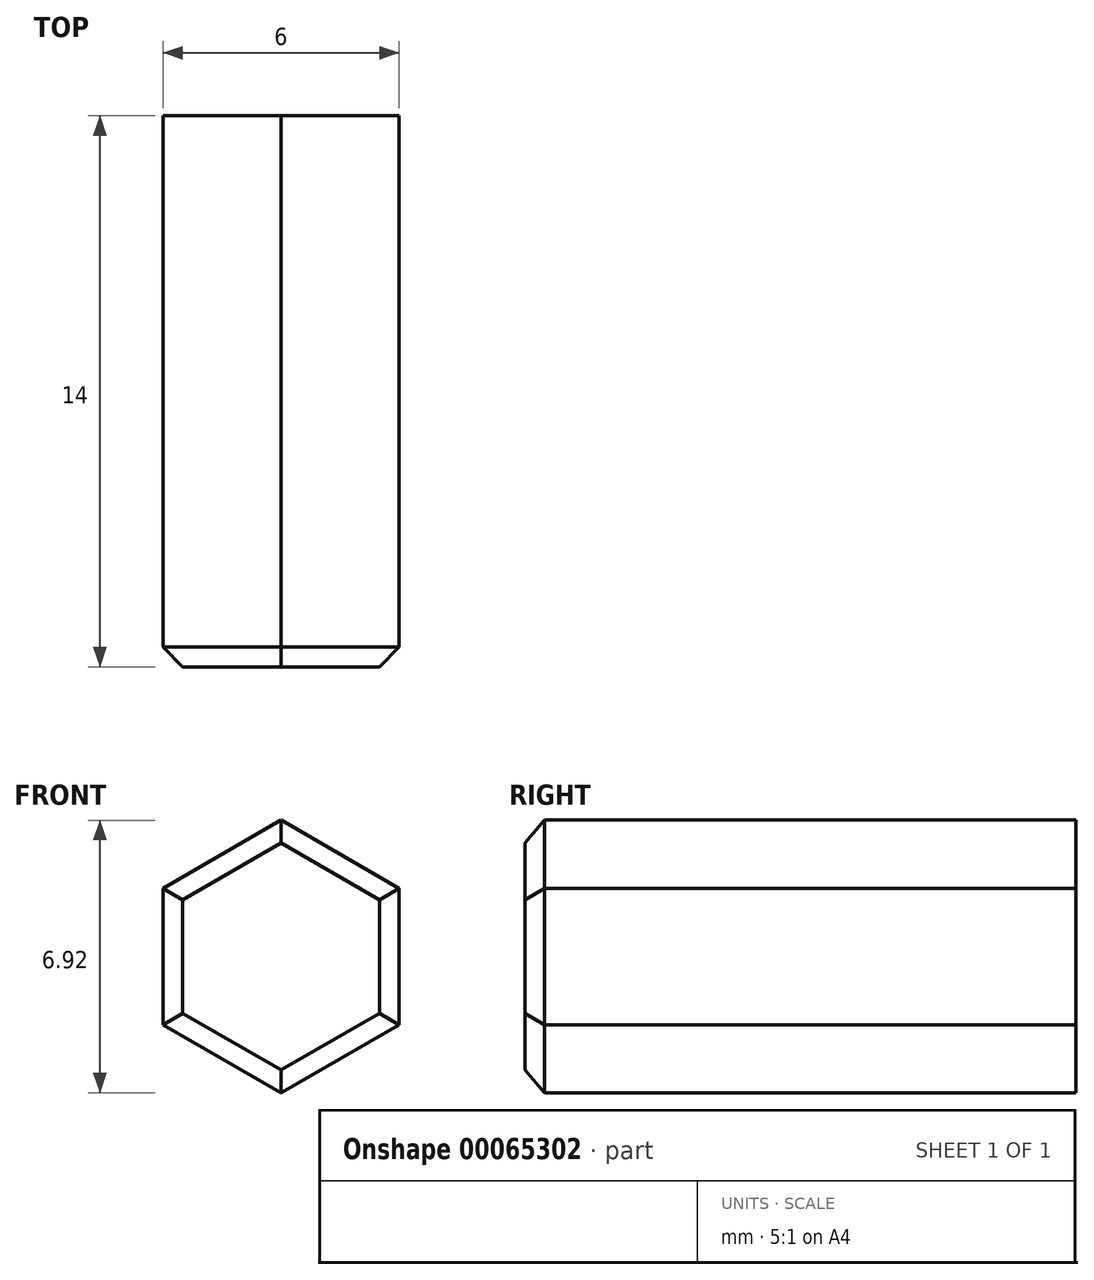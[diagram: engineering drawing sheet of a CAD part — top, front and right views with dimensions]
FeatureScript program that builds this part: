
annotation { "Feature Type Name" : "Feature", "Feature Type Description" : "" }
export const myFeature = defineFeature(function(context is Context, id is Id, definition is map)
    precondition{}
    {
        {
            var Q0;
            Q0=qCreatedBy(makeId("Front.planeOp"),FACE);
            var sketch = newSketch(context, id + "F0", { "sketchPlane" : qUnion([Q0])});
            skCircle(sketch, "E0.cCircle", {"center": v(0, 0) * mm, "radius": 3 * mm, "construction": true});
            skLineSegment(sketch, "E0.0", {"start": v(3, 1.73) * mm, "end": v(3, -1.73) * mm});
            skLineSegment(sketch, "E0.1", {"start": v(3, -1.73) * mm, "end": v(0, -3.46) * mm});
            skLineSegment(sketch, "E0.2", {"start": v(0, -3.46) * mm, "end": v(-3, -1.73) * mm});
            skLineSegment(sketch, "E0.3", {"start": v(-3, -1.73) * mm, "end": v(-3, 1.73) * mm});
            skLineSegment(sketch, "E0.4", {"start": v(-3, 1.73) * mm, "end": v(0, 3.46) * mm});
            skLineSegment(sketch, "E0.5", {"start": v(0, 3.46) * mm, "end": v(3, 1.73) * mm});
            skPoint(sketch, "E0.0.midPoint", {"position": v(3, 0) * mm});
            skSolve(sketch);
        }
        {
            var Q0;
            Q0 = qSketchRegion(id + "F0", true);
            extrude(context, id + "F1", {"entities" : qUnion([Q0]), "depth" : 14 * mm});
        }
        {
            var Q0;
            Q0=makeQuery(id+"F1.opExtrude","CAP_EDGE",EDGE,{"disambiguationData":[OSD([sQuery(id+"F0.wireOp",EDGE,"E0.4")])],"isStart":false});
            var Q1;
            Q1=makeQuery(id+"F1.opExtrude","CAP_EDGE",EDGE,{"disambiguationData":[OSD([sQuery(id+"F0.wireOp",EDGE,"E0.3")])],"isStart":false});
            var Q2;
            Q2=makeQuery(id+"F1.opExtrude","CAP_EDGE",EDGE,{"disambiguationData":[OSD([sQuery(id+"F0.wireOp",EDGE,"E0.2")])],"isStart":false});
            var Q3;
            Q3=makeQuery(id+"F1.opExtrude","CAP_EDGE",EDGE,{"disambiguationData":[OSD([sQuery(id+"F0.wireOp",EDGE,"E0.1")])],"isStart":false});
            var Q4;
            Q4=makeQuery(id+"F1.opExtrude","CAP_EDGE",EDGE,{"disambiguationData":[OSD([sQuery(id+"F0.wireOp",EDGE,"E0.0")])],"isStart":false});
            var Q5;
            Q5=makeQuery(id+"F1.opExtrude","CAP_EDGE",EDGE,{"disambiguationData":[OSD([sQuery(id+"F0.wireOp",EDGE,"E0.5")])],"isStart":false});
            chamfer(context, id + "F2", {"entities" : qUnion([Q0, Q1, Q2, Q3, Q4, Q5]), "width" : 0.5 * mm, "tangentPropagation" : true});
        }
    });
